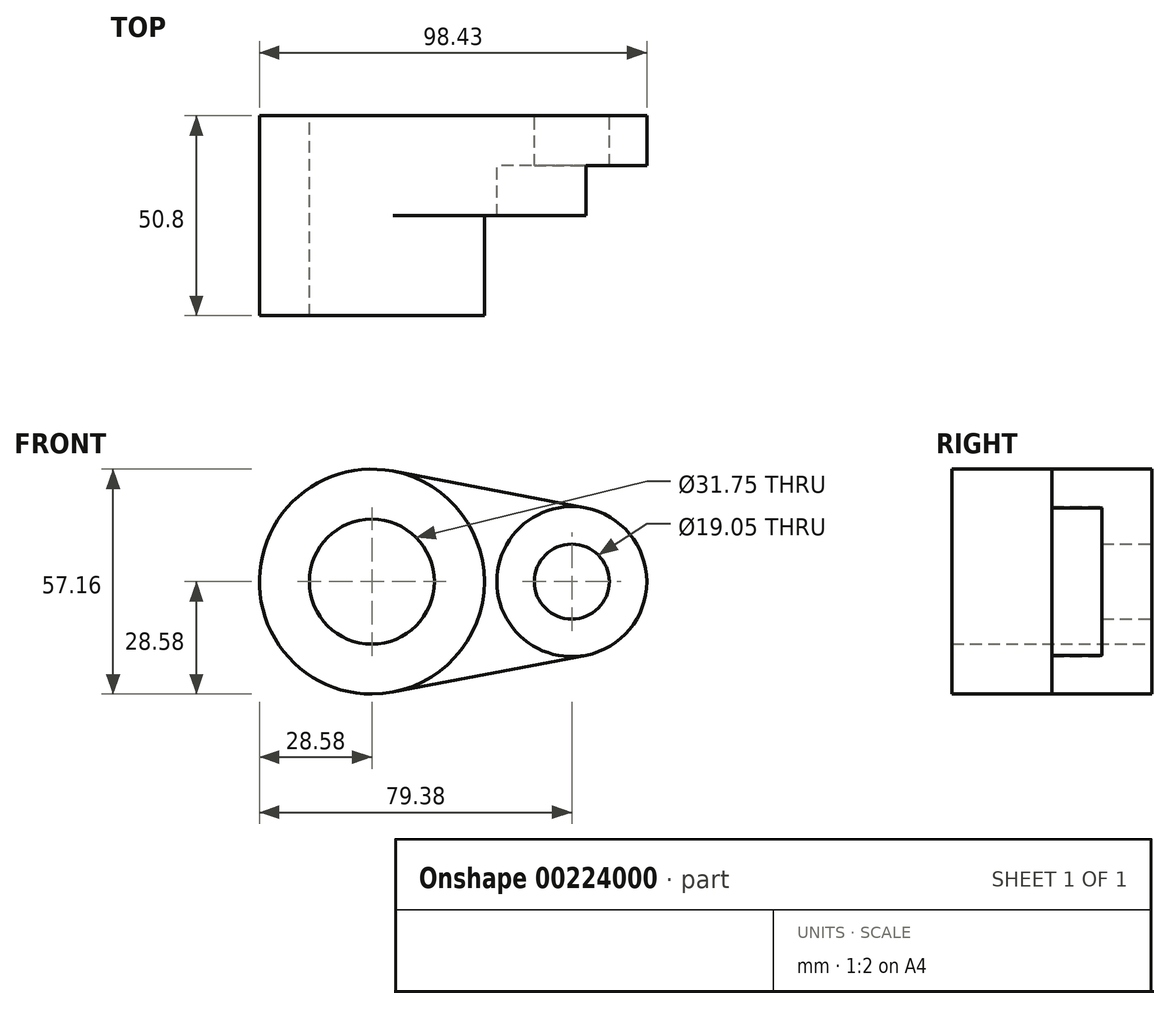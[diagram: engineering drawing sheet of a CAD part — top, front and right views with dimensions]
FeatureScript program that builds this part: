
annotation { "Feature Type Name" : "Feature", "Feature Type Description" : "" }
export const myFeature = defineFeature(function(context is Context, id is Id, definition is map)
    precondition{}
    {
        {
            var Q0;
            Q0=qCreatedBy(makeId("Front.planeOp"),FACE);
            var sketch = newSketch(context, id + "F0", { "sketchPlane" : qUnion([Q0])});
            skCircle(sketch, "E0", {"center": v(0, 0) * mm, "radius": 15.88 * mm});
            skCircle(sketch, "E1", {"center": v(0, 0) * mm, "radius": 28.58 * mm});
            skCircle(sketch, "E2", {"center": v(50.8, 0) * mm, "radius": 9.53 * mm});
            skCircle(sketch, "E3", {"center": v(50.8, 0) * mm, "radius": 19.05 * mm});
            skLineSegment(sketch, "E4", {"start": v(5.36, 28.07) * mm, "end": v(54.37, 18.71) * mm});
            skLineSegment(sketch, "E5", {"start": v(5.36, -28.07) * mm, "end": v(54.37, -18.71) * mm});
            skSolve(sketch);
        }
        {
            var Q0;
            {var subQ0=sQuery(id+"F0.wireOp",EDGE,"E4");Q0=makeQuery(id+"F0.imprint","IMPRINT",FACE,{"disambiguationData":[TD([[makeQuery(id+"F0.imprint","IMPRINT",EDGE,{"derivedFrom":subQ0}),-1.0]])]});}
            extrude(context, id + "F1", {"entities" : qUnion([Q0]), "depth" : 25.4 * mm});
        }
        {
            var Q0;
            Q0=makeQuery(id+"F0.imprint","IMPRINT",FACE,{"disambiguationData":[TD([[makeQuery(id+"F0.imprint","IMPRINT",EDGE,{"derivedFrom":sQuery(id+"F0.wireOp",EDGE,"E0")}),-1.0]])]});
            extrude(context, id + "F2", {"entities" : qUnion([Q0]), "operationType" : NewBodyOperationType.ADD, "depth" : 50.8 * mm});
        }
        {
            var Q0;
            Q0=makeQuery(id+"F0.imprint","IMPRINT",FACE,{"disambiguationData":[TD([[makeQuery(id+"F0.imprint","IMPRINT",EDGE,{"derivedFrom":sQuery(id+"F0.wireOp",EDGE,"E2")}),-1.0]])]});
            extrude(context, id + "F3", {"entities" : qUnion([Q0]), "operationType" : NewBodyOperationType.ADD, "depth" : 12.7 * mm});
        }
    });
